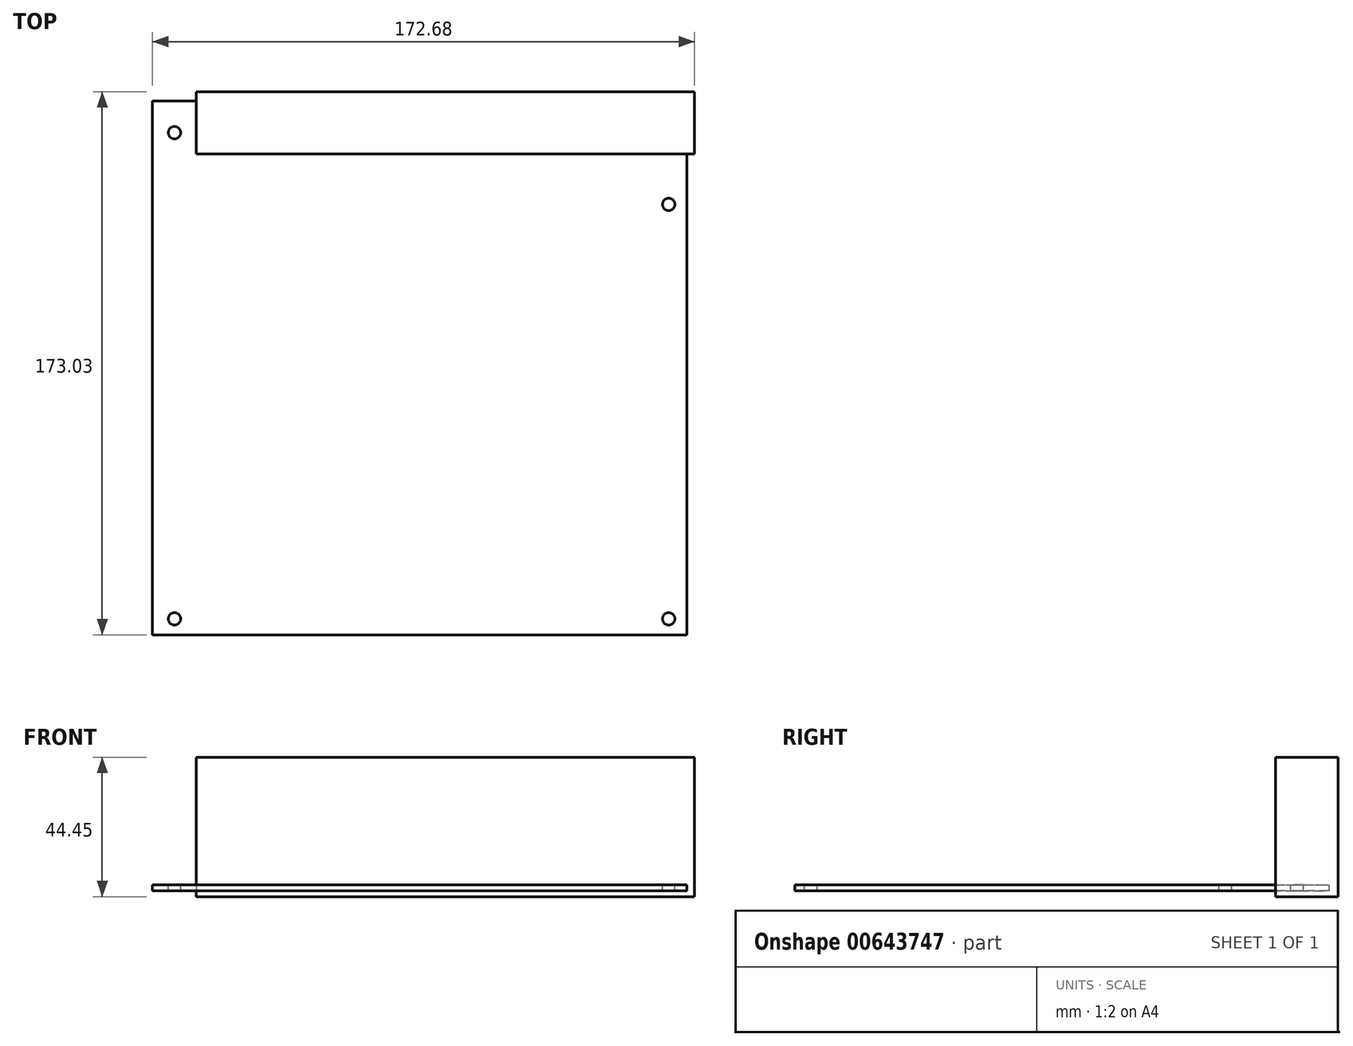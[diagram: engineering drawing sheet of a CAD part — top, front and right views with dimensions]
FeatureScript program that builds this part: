
annotation { "Feature Type Name" : "Feature", "Feature Type Description" : "" }
export const myFeature = defineFeature(function(context is Context, id is Id, definition is map)
    precondition{}
    {
        {
            var Q0;
            Q0=qCreatedBy(makeId("Top.planeOp"),FACE);
            var sketch = newSketch(context, id + "F0", { "sketchPlane" : qUnion([Q0])});
            skLineSegment(sketch, "E0.bottom", {"start": v(-6.99, -5.08) * mm, "end": v(163.2, -5.08) * mm});
            skLineSegment(sketch, "E0.top", {"start": v(-7, 165.1) * mm, "end": v(163.2, 165.1) * mm});
            skLineSegment(sketch, "E0.left", {"start": v(-6.99, -5.08) * mm, "end": v(-7, 165.1) * mm});
            skLineSegment(sketch, "E0.right", {"start": v(163.2, -5.08) * mm, "end": v(163.2, 165.1) * mm});
            skCircle(sketch, "E1", {"center": v(0, 0) * mm, "radius": 1.98 * mm});
            skCircle(sketch, "E2", {"center": v(157.48, 0) * mm, "radius": 1.98 * mm});
            skCircle(sketch, "E3", {"center": v(0, 154.94) * mm, "radius": 1.98 * mm});
            skCircle(sketch, "E4", {"center": v(157.48, 132.08) * mm, "radius": 1.98 * mm});
            skLineSegment(sketch, "E5.bottom", {"start": v(6.9, 167.95) * mm, "end": v(165.7, 167.95) * mm});
            skLineSegment(sketch, "E5.top", {"start": v(6.9, 148.1) * mm, "end": v(165.7, 148.1) * mm});
            skLineSegment(sketch, "E5.left", {"start": v(6.9, 167.95) * mm, "end": v(6.9, 148.1) * mm});
            skLineSegment(sketch, "E5.right", {"start": v(165.7, 167.95) * mm, "end": v(165.7, 148.1) * mm});
            skSolve(sketch);
        }
        {
            var Q0;
            {var subQ1=sQuery(id+"F0.wireOp",EDGE,"E0.bottom");Q0=makeQuery(id+"F0.imprint","IMPRINT",FACE,{"disambiguationData":[TD([[makeQuery(id+"F0.imprint","IMPRINT",EDGE,{"derivedFrom":subQ1}),1.0]])]});}
            var Q1;
            {var subQ0=sQuery(id+"F0.wireOp",EDGE,"E0.right");var subQ1=sQuery(id+"F0.wireOp",EDGE,"E0.top");var subQ2=makeQuery(id+"F0.imprint","INTERSECT",VERTEX,{"derivedFrom":[subQ1,subQ0]});Q1=makeQuery(id+"F0.imprint","IMPRINT",FACE,{"disambiguationData":[TD([[makeQuery(id+"F0.imprint","IMPRINT",EDGE,{"disambiguationData":[TD([[subQ2,1.0]])],"derivedFrom":subQ1}),-1.0]])]});}
            extrude(context, id + "F1", {"entities" : qUnion([Q0, Q1]), "oppositeDirection" : true, "depth" : 2 * mm, "offsetDistance" : 25 * mm});
        }
        {
            var Q0;
            {var subQ0=sQuery(id+"F0.wireOp",EDGE,"E0.right");var subQ1=sQuery(id+"F0.wireOp",EDGE,"E0.top");var subQ2=makeQuery(id+"F0.imprint","INTERSECT",VERTEX,{"derivedFrom":[subQ1,subQ0]});Q0=makeQuery(id+"F0.imprint","IMPRINT",FACE,{"disambiguationData":[TD([[makeQuery(id+"F0.imprint","IMPRINT",EDGE,{"disambiguationData":[TD([[subQ2,1.0]])],"derivedFrom":subQ1}),-1.0]])]});}
            var Q1;
            {var subQ0=sQuery(id+"F0.wireOp",EDGE,"E5.bottom");Q1=makeQuery(id+"F0.imprint","IMPRINT",FACE,{"disambiguationData":[TD([[makeQuery(id+"F0.imprint","IMPRINT",EDGE,{"derivedFrom":subQ0}),-1.0]])]});}
            extrude(context, id + "F2", {"entities" : qUnion([Q0, Q1]), "operationType" : NewBodyOperationType.ADD, "oppositeDirection" : true, "depth" : 3.81 * mm, "offsetDistance" : 25 * mm});
        }
        {
            var Q0;
            Q0=makeQuery(id+"F2.opExtrude","CAP_FACE",FACE,{"disambiguationData":[OSD([sQuery(id+"F0.wireOp",EDGE,"E5.bottom"),sQuery(id+"F0.wireOp",EDGE,"E5.top"),sQuery(id+"F0.wireOp",EDGE,"E5.left"),sQuery(id+"F0.wireOp",EDGE,"E5.right")])],"isStart":false});
            extrude(context, id + "F3", {"entities" : qUnion([Q0]), "operationType" : NewBodyOperationType.ADD, "oppositeDirection" : true, "depth" : 44.45 * mm, "offsetDistance" : 25 * mm});
        }
    });
